# Revit family: DF_ДержательЗажим_Пруток-Пруток_Оцинк_СБетоном_71915_EZETEK
name_source: partatom
category: Соединительные детали воздуховодов
revit_build: Autodesk Revit 2017 (Build: 20170118_1100(x64)
units: mm (PartAtom-declared; Revit-internal decimal feet)

## family parameters
Всегда вертикально = Да
На основе рабочей плоскости = Нет
Общий = Нет
При загрузке вырезать с полостями = Нет
Размер круглого соединителя = Использовать радиус
Тип детали = Крестовина

## types (1)
- ДержательЗажим_Пруток-Пруток_Оцинк_СБетоном_71915
    ADSK_Версия Revit = 2017
    ADSK_Единица измерения = Неспецифицируемое
    ADSK_Завод-изготовитель = Неспецифицируемое
    ADSK_Код изделия = Неспецифицируемое
    ADSK_Количество = 0
    ADSK_Марка = Неспецифицируемое
    ADSK_Масса = 0
    ADSK_Масса_Текст = Неспецифицируемое
    ADSK_Материал = BIMLIB_Сталь_Оцинкованная_EZETEK
    ADSK_Наименование = Неспецифицируемое
    ADSK_Обозначение = Неспецифицируемое
    URL = https://ezetek.ru
    Группа модели = Держатели
    Изготовитель = Ezetek
    Описание = Держатель-зажим применяется для закрепления прутков молниезащитной сетки диаметром 8-10 мм на плоских кровлях. Изделие выполнено на основе бетонного утяжелителя массой 1 кг. Проводники надежно закрепляются на кровле под собственным весом утяжелителя. В состав изделия входит зажим из оцинкованной стали для соединения прутка в перпендикулярном направлении, в параллельном направлении, а также под произвольным углом с помощью болтового соединения. Для крепления изделия возможно применение клеевых составов (жидкие гвозди и т.п.).
    Тип = FA_ДержательЗажим_Пруток-Пруток_Оцинк_СБетоном_71915_EZETEK : ДержательЗажим_Пруток-Пруток_Оцинк_СБетоном_71915
    Угол = 90.00°
